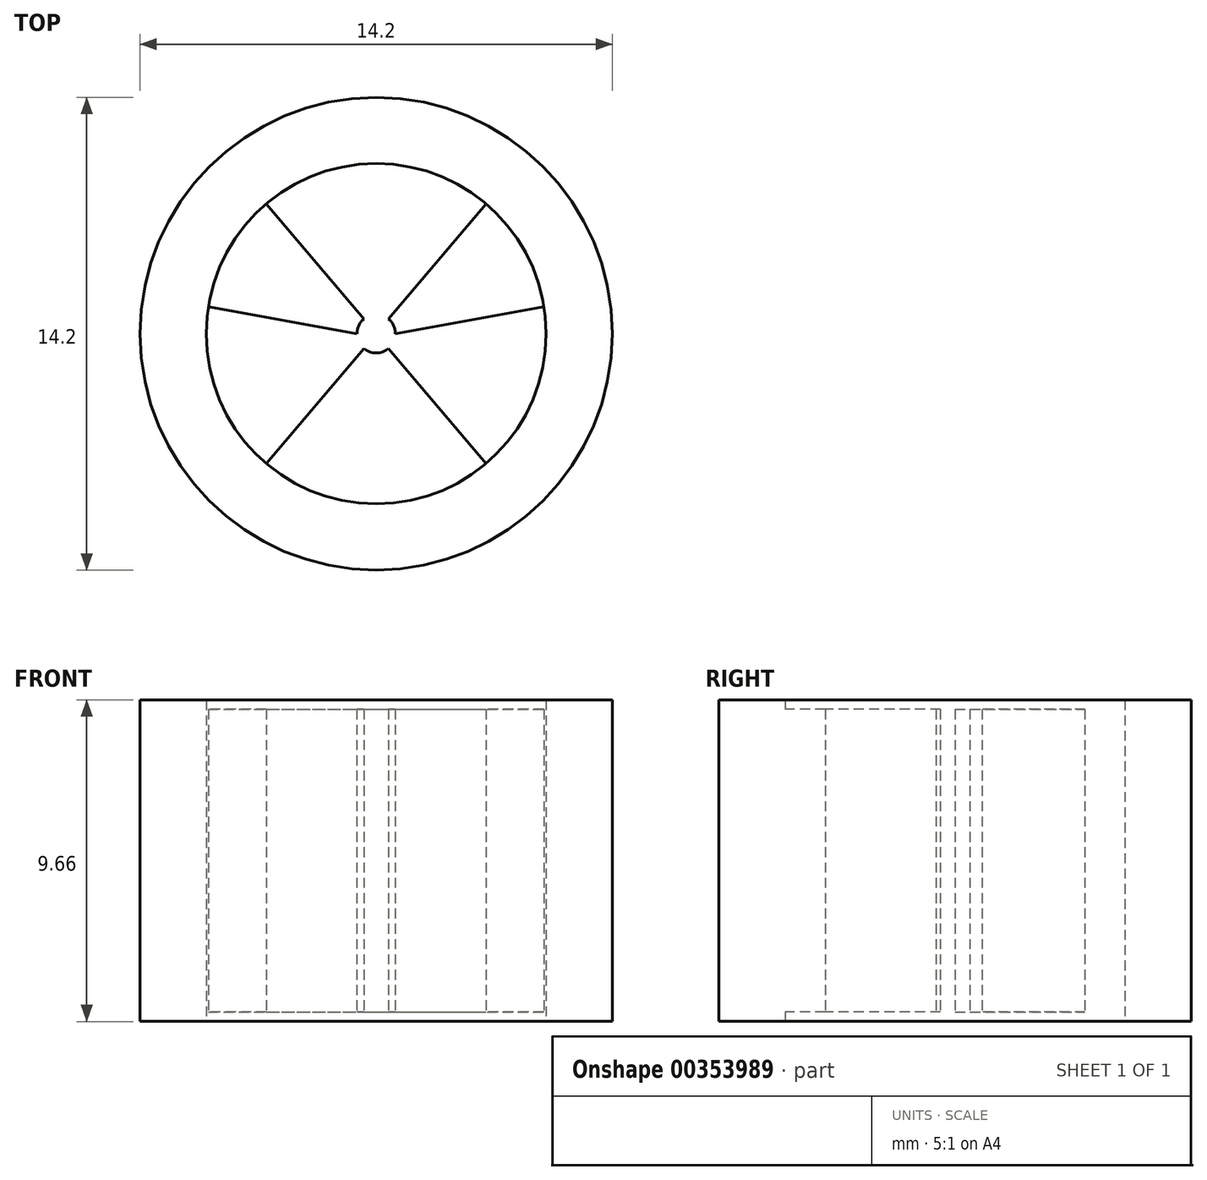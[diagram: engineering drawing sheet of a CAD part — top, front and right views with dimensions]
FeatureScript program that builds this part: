
annotation { "Feature Type Name" : "Feature", "Feature Type Description" : "" }
export const myFeature = defineFeature(function(context is Context, id is Id, definition is map)
    precondition{}
    {
        {
            var Q0;
            Q0=qCreatedBy(makeId("Top.planeOp"),FACE);
            var sketch = newSketch(context, id + "F0", { "sketchPlane" : qUnion([Q0])});
            skCircle(sketch, "E0", {"center": v(0, 0) * mm, "radius": 0.58 * mm});
            skCircle(sketch, "E1", {"center": v(0, 0) * mm, "radius": 5.11 * mm});
            skCircle(sketch, "E2", {"center": v(0, 0) * mm, "radius": 7.1 * mm});
            skLineSegment(sketch, "E3", {"start": v(-5.05, 0.81) * mm, "end": v(-0.58, 0) * mm});
            skLineSegment(sketch, "E4", {"start": v(-3.3, 3.9) * mm, "end": v(-0.37, 0.44) * mm});
            skLineSegment(sketch, "E5", {"start": v(0.37, 0.44) * mm, "end": v(3.3, 3.9) * mm});
            skLineSegment(sketch, "E6", {"start": v(0.58, 0) * mm, "end": v(5.05, 0.81) * mm});
            skLineSegment(sketch, "E7", {"start": v(0.37, -0.44) * mm, "end": v(3.3, -3.9) * mm});
            skLineSegment(sketch, "E8", {"start": v(-0.37, -0.44) * mm, "end": v(-3.3, -3.9) * mm});
            skSolve(sketch);
        }
        {
            var Q0;
            Q0=makeQuery(id+"F0.imprint","IMPRINT",FACE,{"disambiguationData":[TD([[makeQuery(id+"F0.imprint","IMPRINT",EDGE,{"derivedFrom":sQuery(id+"F0.wireOp",EDGE,"E2")}),1.0]])]});
            extrude(context, id + "F1", {"entities" : qUnion([Q0]), "endBound" : BoundingType.SYMMETRIC, "depth" : 9.65 * mm});
        }
        {
            var Q0;
            {var subQ0=sQuery(id+"F0.wireOp",EDGE,"E5");Q0=makeQuery(id+"F0.imprint","IMPRINT",FACE,{"disambiguationData":[TD([[makeQuery(id+"F0.imprint","IMPRINT",EDGE,{"derivedFrom":subQ0}),-1.0]])]});}
            var Q1;
            {var subQ0=sQuery(id+"F0.wireOp",EDGE,"E3");Q1=makeQuery(id+"F0.imprint","IMPRINT",FACE,{"disambiguationData":[TD([[makeQuery(id+"F0.imprint","IMPRINT",EDGE,{"derivedFrom":subQ0}),1.0]])]});}
            var Q2;
            {var subQ0=sQuery(id+"F0.wireOp",EDGE,"E7");Q2=makeQuery(id+"F0.imprint","IMPRINT",FACE,{"disambiguationData":[TD([[makeQuery(id+"F0.imprint","IMPRINT",EDGE,{"derivedFrom":subQ0}),-1.0]])]});}
            extrude(context, id + "F2", {"entities" : qUnion([Q0, Q1, Q2]), "operationType" : NewBodyOperationType.ADD, "endBound" : BoundingType.SYMMETRIC, "depth" : 9.1 * mm});
        }
        {
            var Q0;
            Q0=sQuery(id+"F0.wireOp",EDGE,"E0");
            extrude(context, id + "F3", {"bodyType" : ToolBodyType.SURFACE, "surfaceEntities" : qUnion([Q0]), "endBound" : BoundingType.SYMMETRIC, "depth" : 9.25 * mm});
        }
    });
